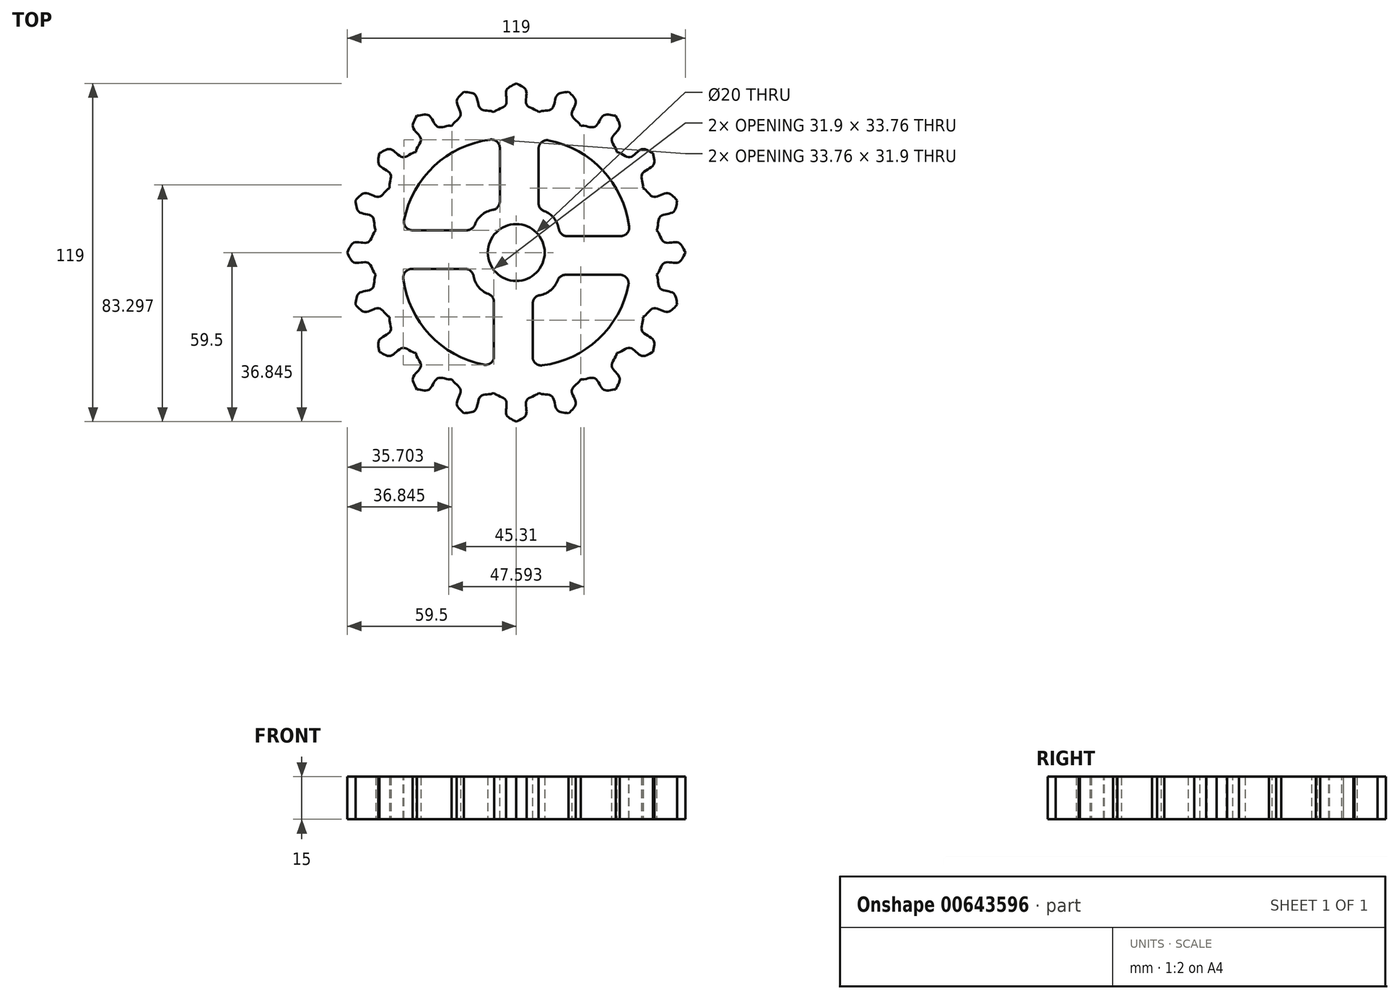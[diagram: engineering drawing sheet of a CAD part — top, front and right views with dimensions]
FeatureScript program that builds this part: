
annotation { "Feature Type Name" : "Feature", "Feature Type Description" : "" }
export const myFeature = defineFeature(function(context is Context, id is Id, definition is map)
    precondition{}
    {
        {
            var Q0;
            Q0=qCreatedBy(makeId("Top.planeOp"),FACE);
            var sketch = newSketch(context, id + "F0", { "sketchPlane" : qUnion([Q0])});
            skCircle(sketch, "E0", {"center": v(0, 0) * mm, "radius": 10 * mm});
            skCircle(sketch, "E1", {"center": v(0, 0) * mm, "radius": 50 * mm});
            skFitSpline(sketch, "E2", {"points": [v(0, 59.5) * mm, v(3.5, 57) * mm, v(3.7, 52) * mm, v(7.85, 49.38) * mm], "startDerivative": vector(12.7, -6.54) * mm, "endDerivative": vector(7.85, -9.96) * mm});
            skFitSpline(sketch, "E3.MirrorCS", {"points": [v(0, 59.5) * mm, v(-3.5, 57) * mm, v(-3.7, 52) * mm, v(-7.85, 49.38) * mm], "startDerivative": vector(-12.7, -6.54) * mm, "endDerivative": vector(-7.85, -9.96) * mm});
            skSolve(sketch);
        }
        {
            var Q0;
            Q0 = qSketchRegion(id + "F0", true);
            extrude(context, id + "F1", {"entities" : qUnion([Q0]), "depth" : 15 * mm, "offsetDistance" : 25 * mm});
        }
        {
            var Q0;
            Q0=makeQuery(id+"F1.opExtrude","CAP_FACE",FACE,{"disambiguationData":[OSD([sQuery(id+"F0.wireOp",EDGE,"E0"),sQuery(id+"F0.wireOp",EDGE,"E1"),sQuery(id+"F0.wireOp",EDGE,"E2"),sQuery(id+"F0.wireOp",EDGE,"E3.MirrorCS")])],"isStart":false});
            var sketch = newSketch(context, id + "F2", { "sketchPlane" : qUnion([Q0])});
            skLineSegment(sketch, "E4", {"start": v(7.85, 36.54) * mm, "end": v(7.85, 17.38) * mm});
            skLineSegment(sketch, "E5", {"start": v(17.96, 5.77) * mm, "end": v(36.76, 5.77) * mm});
            skArc(sketch, "E6", {"start": v(15, 8.3) * mm, "mid": v(13.27, 12.13) * mm, "end": v(9.82, 14.56) * mm});
            skArc(sketch, "E7", {"start": v(39.73, 9.15) * mm, "mid": v(30.48, 28.89) * mm, "end": v(11.43, 39.48) * mm});
            skPoint(sketch, "E8.visualSharp", {"position": v(7.85, 40) * mm});
            skArc(sketch, "E8.filletArc", {"start": v(11.43, 39.48) * mm, "mid": v(8.94, 38.86) * mm, "end": v(7.85, 36.54) * mm});
            skPoint(sketch, "E9.visualSharp", {"position": v(7.85, 15) * mm});
            skArc(sketch, "E9.filletArc", {"start": v(7.85, 17.38) * mm, "mid": v(8.39, 15.66) * mm, "end": v(9.82, 14.56) * mm});
            skPoint(sketch, "E10.visualSharp", {"position": v(15, 5.77) * mm});
            skArc(sketch, "E10.filletArc", {"start": v(15, 8.3) * mm, "mid": v(16.02, 6.5) * mm, "end": v(17.96, 5.77) * mm});
            skPoint(sketch, "E11.visualSharp", {"position": v(40, 5.77) * mm});
            skArc(sketch, "E11.filletArc", {"start": v(36.76, 5.77) * mm, "mid": v(39, 6.79) * mm, "end": v(39.73, 9.15) * mm});
            skArc(sketch, "E12.1.0", {"start": v(-9.15, 39.73) * mm, "mid": v(-28.89, 30.48) * mm, "end": v(-39.48, 11.43) * mm});
            skLineSegment(sketch, "E12.1.1", {"start": v(-36.54, 7.85) * mm, "end": v(-17.38, 7.85) * mm});
            skArc(sketch, "E12.1.2", {"start": v(-8.3, 15) * mm, "mid": v(-12.13, 13.27) * mm, "end": v(-14.56, 9.82) * mm});
            skLineSegment(sketch, "E12.1.3", {"start": v(-5.77, 17.96) * mm, "end": v(-5.77, 36.76) * mm});
            skPoint(sketch, "E12.1.4", {"position": v(-5.77, 40) * mm});
            skArc(sketch, "E12.1.5", {"start": v(-5.77, 36.76) * mm, "mid": v(-6.79, 39) * mm, "end": v(-9.15, 39.73) * mm});
            skArc(sketch, "E12.1.6", {"start": v(-8.3, 15) * mm, "mid": v(-6.5, 16.02) * mm, "end": v(-5.77, 17.96) * mm});
            skArc(sketch, "E12.1.7", {"start": v(-17.38, 7.85) * mm, "mid": v(-15.66, 8.39) * mm, "end": v(-14.56, 9.82) * mm});
            skArc(sketch, "E12.1.8", {"start": v(-39.48, 11.43) * mm, "mid": v(-38.86, 8.94) * mm, "end": v(-36.54, 7.85) * mm});
            skArc(sketch, "E12.2.0", {"start": v(-39.73, -9.15) * mm, "mid": v(-30.48, -28.89) * mm, "end": v(-11.43, -39.48) * mm});
            skLineSegment(sketch, "E12.2.1", {"start": v(-7.85, -36.54) * mm, "end": v(-7.85, -17.38) * mm});
            skArc(sketch, "E12.2.2", {"start": v(-15, -8.3) * mm, "mid": v(-13.27, -12.13) * mm, "end": v(-9.82, -14.56) * mm});
            skLineSegment(sketch, "E12.2.3", {"start": v(-17.96, -5.77) * mm, "end": v(-36.76, -5.77) * mm});
            skPoint(sketch, "E12.2.4", {"position": v(-40, -5.77) * mm});
            skArc(sketch, "E12.2.5", {"start": v(-36.76, -5.77) * mm, "mid": v(-39, -6.79) * mm, "end": v(-39.73, -9.15) * mm});
            skArc(sketch, "E12.2.6", {"start": v(-15, -8.3) * mm, "mid": v(-16.02, -6.5) * mm, "end": v(-17.96, -5.77) * mm});
            skArc(sketch, "E12.2.7", {"start": v(-7.85, -17.38) * mm, "mid": v(-8.39, -15.66) * mm, "end": v(-9.82, -14.56) * mm});
            skArc(sketch, "E12.2.8", {"start": v(-11.43, -39.48) * mm, "mid": v(-8.94, -38.86) * mm, "end": v(-7.85, -36.54) * mm});
            skArc(sketch, "E12.3.0", {"start": v(9.15, -39.73) * mm, "mid": v(28.89, -30.48) * mm, "end": v(39.48, -11.43) * mm});
            skLineSegment(sketch, "E12.3.1", {"start": v(36.54, -7.85) * mm, "end": v(17.38, -7.85) * mm});
            skArc(sketch, "E12.3.2", {"start": v(8.3, -15) * mm, "mid": v(12.13, -13.27) * mm, "end": v(14.56, -9.82) * mm});
            skLineSegment(sketch, "E12.3.3", {"start": v(5.77, -17.96) * mm, "end": v(5.77, -36.76) * mm});
            skPoint(sketch, "E12.3.4", {"position": v(5.77, -40) * mm});
            skArc(sketch, "E12.3.5", {"start": v(5.77, -36.76) * mm, "mid": v(6.79, -39) * mm, "end": v(9.15, -39.73) * mm});
            skArc(sketch, "E12.3.6", {"start": v(8.3, -15) * mm, "mid": v(6.5, -16.02) * mm, "end": v(5.77, -17.96) * mm});
            skArc(sketch, "E12.3.7", {"start": v(17.38, -7.85) * mm, "mid": v(15.66, -8.39) * mm, "end": v(14.56, -9.82) * mm});
            skArc(sketch, "E12.3.8", {"start": v(39.48, -11.43) * mm, "mid": v(38.86, -8.94) * mm, "end": v(36.54, -7.85) * mm});
            skPoint(sketch, "E12.center", {"position": v(0, 0) * mm});
            skSolve(sketch);
        }
        {
            var Q0;
            Q0=makeQuery(id+"F1.opExtrude","SWEPT_BODY",BODY,{"disambiguationData":[OSD([sQuery(id+"F0.wireOp",EDGE,"E0"),sQuery(id+"F0.wireOp",EDGE,"E1"),sQuery(id+"F0.wireOp",EDGE,"E2"),sQuery(id+"F0.wireOp",EDGE,"E3.MirrorCS")])]});
            var Q1;
            Q1=makeQuery(id+"F1.opExtrude","CAP_EDGE",EDGE,{"disambiguationData":[OSD([sQuery(id+"F0.wireOp",EDGE,"E0")])],"isStart":false});
            circularPattern(context, id + "F3", {"operationType" : NewBodyOperationType.ADD, "entities" : qUnion([Q0]), "axis" : qUnion([Q1]), "angle" : 360 * degree, "instanceCount" : 20, "equalSpace" : true});
        }
        {
            var Q0;
            Q0 = qSketchRegion(id + "F2", true);
            var Q1;
            Q1=makeQuery(id+"F2.imprint","IMPRINT",FACE,{"disambiguationData":[TD([[makeQuery(id+"F2.imprint","IMPRINT",EDGE,{"derivedFrom":makeQuery(id+"F1.opExtrude","CAP_EDGE",EDGE,{"disambiguationData":[OSD([sQuery(id+"F0.wireOp",EDGE,"E0")])],"isStart":false})}),1.0]])]});
            extrude(context, id + "F4", {"entities" : qUnion([Q0, Q1]), "operationType" : NewBodyOperationType.REMOVE, "oppositeDirection" : true, "depth" : 25 * mm, "offsetDistance" : 25 * mm});
        }
    });
